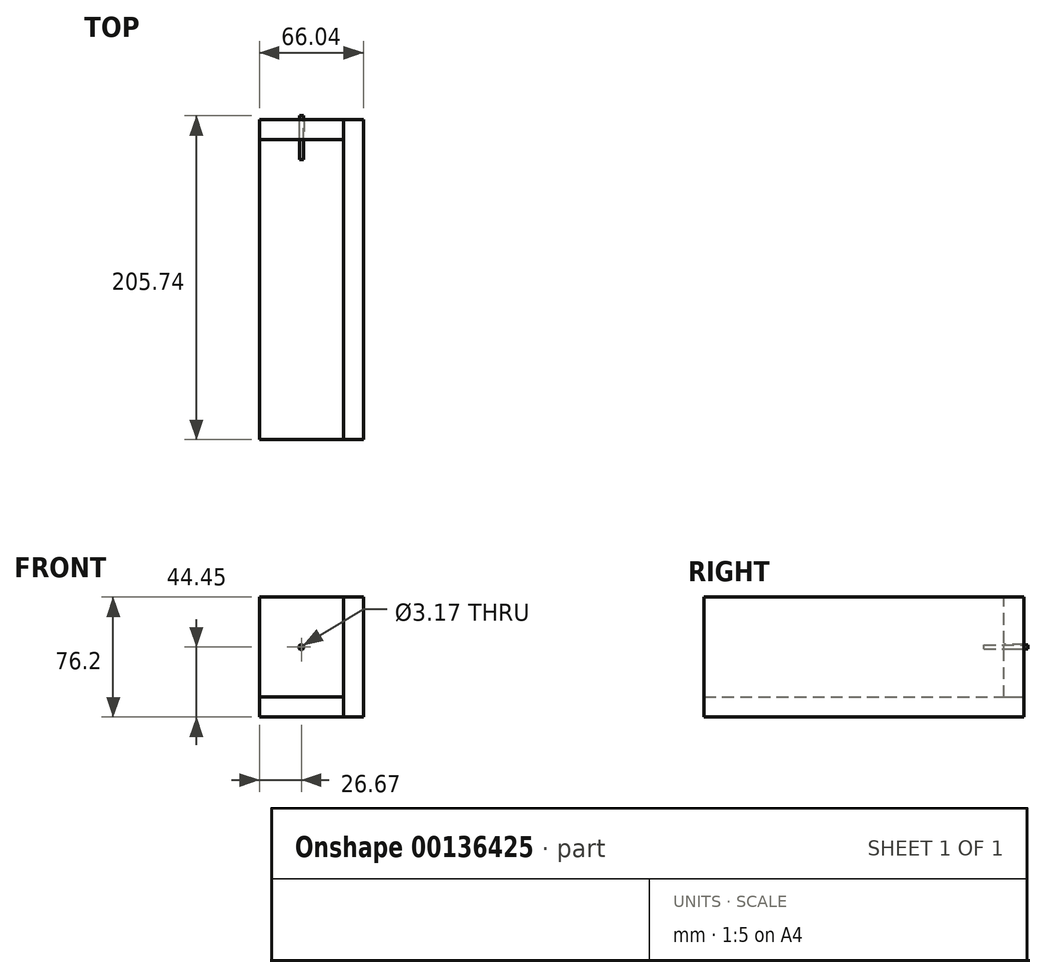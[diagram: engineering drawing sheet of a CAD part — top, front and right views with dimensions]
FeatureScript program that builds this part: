
annotation { "Feature Type Name" : "Feature", "Feature Type Description" : "" }
export const myFeature = defineFeature(function(context is Context, id is Id, definition is map)
    precondition{}
    {
        {
            var Q0;
            Q0=qCreatedBy(makeId("Front.planeOp"),FACE);
            var sketch = newSketch(context, id + "F0", { "sketchPlane" : qUnion([Q0])});
            skLineSegment(sketch, "E0.bottom", {"start": v(26.67, 0) * mm, "end": v(-26.67, 0) * mm});
            skLineSegment(sketch, "E0.top", {"start": v(26.67, 63.5) * mm, "end": v(-26.67, 63.5) * mm});
            skLineSegment(sketch, "E0.left", {"start": v(26.67, 0) * mm, "end": v(26.67, 63.5) * mm});
            skLineSegment(sketch, "E0.right", {"start": v(-26.67, 0) * mm, "end": v(-26.67, 63.5) * mm});
            skPoint(sketch, "E0.middle", {"position": v(0, 31.75) * mm});
            skSolve(sketch);
        }
        {
            var Q0;
            Q0 = qSketchRegion(id + "F0", true);
            extrude(context, id + "F1", {"entities" : qUnion([Q0]), "depth" : 12.7 * mm});
        }
        {
            var Q0;
            Q0=qCreatedBy(makeId("Front.planeOp"),FACE);
            var sketch = newSketch(context, id + "F2", { "sketchPlane" : qUnion([Q0])});
            skLineSegment(sketch, "E1.bottom", {"start": v(26.67, -12.7) * mm, "end": v(39.37, -12.7) * mm});
            skLineSegment(sketch, "E1.top", {"start": v(26.67, 63.5) * mm, "end": v(39.37, 63.5) * mm});
            skLineSegment(sketch, "E1.left", {"start": v(26.67, -12.7) * mm, "end": v(26.67, 63.5) * mm});
            skLineSegment(sketch, "E1.right", {"start": v(39.37, -12.7) * mm, "end": v(39.37, 63.5) * mm});
            skPoint(sketch, "E1.middle", {"position": v(33.02, 25.4) * mm});
            skSolve(sketch);
        }
        {
            var Q0;
            Q0 = qSketchRegion(id + "F2", true);
            extrude(context, id + "F3", {"entities" : qUnion([Q0]), "depth" : 203.2 * mm});
        }
        {
            var Q0;
            Q0=qCreatedBy(makeId("Front.planeOp"),FACE);
            var sketch = newSketch(context, id + "F4", { "sketchPlane" : qUnion([Q0])});
            skLineSegment(sketch, "E2.bottom", {"start": v(26.67, -12.7) * mm, "end": v(-26.67, -12.7) * mm});
            skLineSegment(sketch, "E2.top", {"start": v(26.67, 0) * mm, "end": v(-26.67, 0) * mm});
            skLineSegment(sketch, "E2.left", {"start": v(26.67, -12.7) * mm, "end": v(26.67, 0) * mm});
            skLineSegment(sketch, "E2.right", {"start": v(-26.67, -12.7) * mm, "end": v(-26.67, 0) * mm});
            skPoint(sketch, "E2.middle", {"position": v(0, -6.35) * mm});
            skSolve(sketch);
        }
        {
            var Q0;
            Q0 = qSketchRegion(id + "F4", true);
            var Q1;
            Q1=makeQuery(id+"F3.opExtrude","CAP_FACE",FACE,{"disambiguationData":[OSD([sQuery(id+"F2.wireOp",EDGE,"E1.bottom"),sQuery(id+"F2.wireOp",EDGE,"E1.top"),sQuery(id+"F2.wireOp",EDGE,"E1.left"),sQuery(id+"F2.wireOp",EDGE,"E1.right")])],"isStart":false});
            extrude(context, id + "F5", {"entities" : qUnion([Q0]), "endBound" : BoundingType.UP_TO_SURFACE, "endBoundEntityFace" : qUnion([Q1]), "depth" : 25.4 * mm});
        }
        {
            var Q0;
            Q0=makeQuery(id+"F1.opExtrude","CAP_FACE",FACE,{"disambiguationData":[OSD([sQuery(id+"F0.wireOp",EDGE,"E0.bottom"),sQuery(id+"F0.wireOp",EDGE,"E0.top"),sQuery(id+"F0.wireOp",EDGE,"E0.left"),sQuery(id+"F0.wireOp",EDGE,"E0.right")])],"isStart":false});
            var sketch = newSketch(context, id + "F6", { "sketchPlane" : qUnion([Q0])});
            skCircle(sketch, "E3", {"center": v(0, 31.75) * mm, "radius": 1.59 * mm});
            skPoint(sketch, "E3.centerSnap0", {"position": v(-26.67, 31.75) * mm});
            skSolve(sketch);
        }
        {
            var Q0;
            Q0 = qSketchRegion(id + "F6", true);
            extrude(context, id + "F7", {"entities" : qUnion([Q0]), "operationType" : NewBodyOperationType.REMOVE, "endBound" : BoundingType.THROUGH_ALL, "oppositeDirection" : true, "depth" : 25.4 * mm});
        }
        {
            var Q0;
            Q0=makeQuery(id+"F1.opExtrude","CAP_FACE",FACE,{"disambiguationData":[OSD([sQuery(id+"F0.wireOp",EDGE,"E0.bottom"),sQuery(id+"F0.wireOp",EDGE,"E0.top"),sQuery(id+"F0.wireOp",EDGE,"E0.left"),sQuery(id+"F0.wireOp",EDGE,"E0.right")])],"isStart":false});
            var sketch = newSketch(context, id + "F8", { "sketchPlane" : qUnion([Q0])});
            skCircle(sketch, "E4", {"center": v(0, 31.75) * mm, "radius": 1.27 * mm});
            skSolve(sketch);
        }
        {
            var Q0;
            Q0 = qSketchRegion(id + "F8", true);
            extrude(context, id + "F9", {"entities" : qUnion([Q0]), "depth" : 12.7 * mm, "hasSecondDirection" : true, "secondDirectionOppositeDirection" : true, "secondDirectionDepth" : 15.24 * mm});
        }
    });
